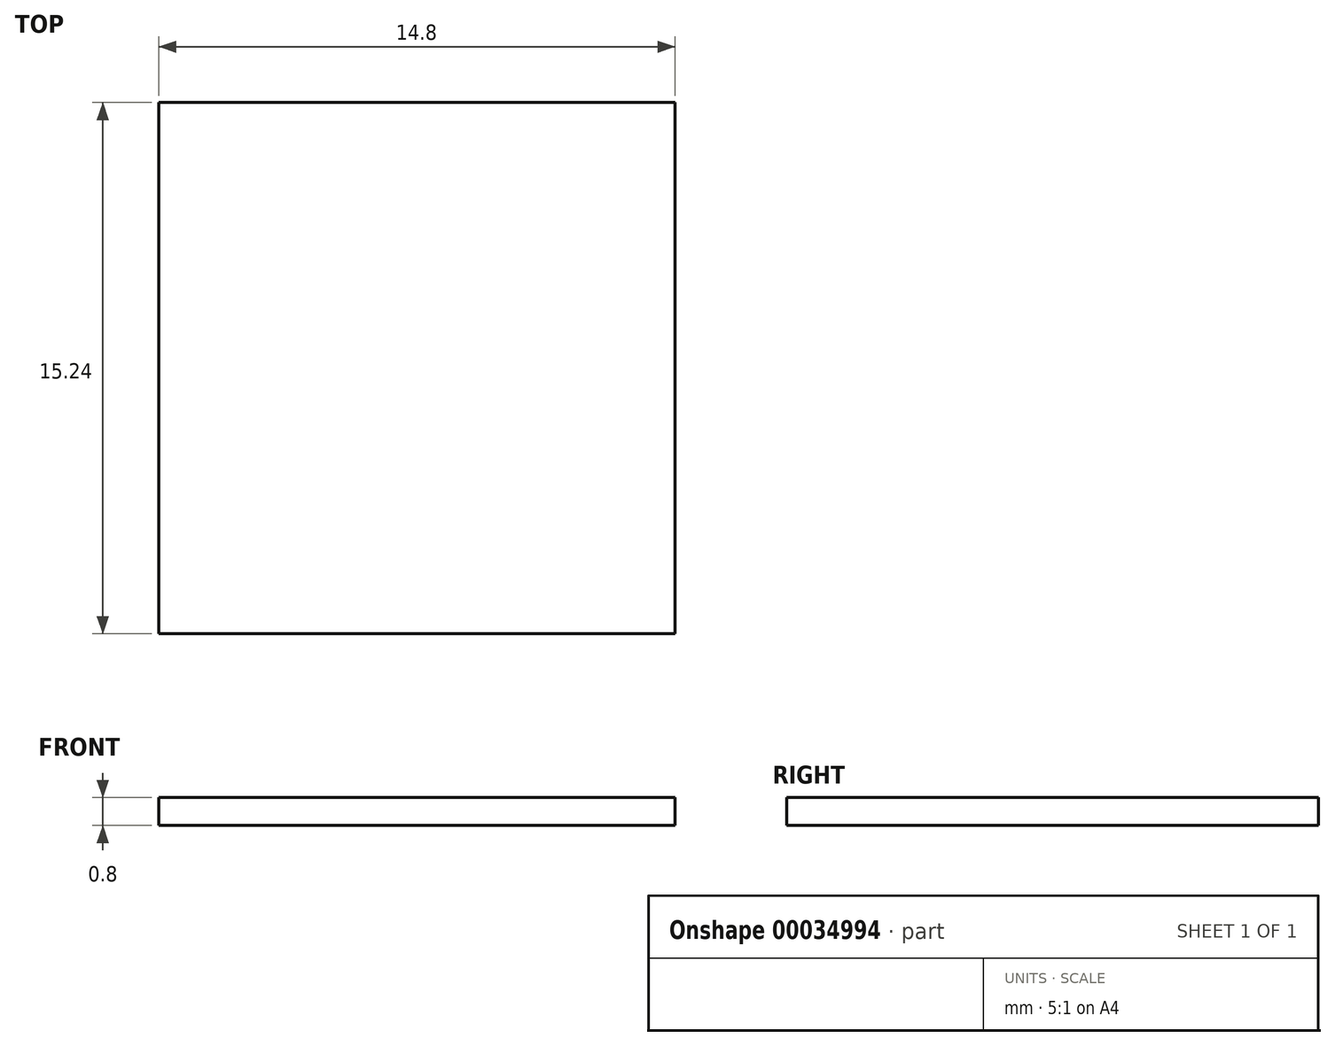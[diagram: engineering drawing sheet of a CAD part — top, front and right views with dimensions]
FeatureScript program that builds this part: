
annotation { "Feature Type Name" : "Feature", "Feature Type Description" : "" }
export const myFeature = defineFeature(function(context is Context, id is Id, definition is map)
    precondition{}
    {
        {
            var Q0;
            Q0=qCreatedBy(makeId("Top.planeOp"),FACE);
            var sketch = newSketch(context, id + "F0", { "sketchPlane" : qUnion([Q0])});
            skLineSegment(sketch, "E0.rect.bottom", {"start": v(7.4, -7.62) * mm, "end": v(-7.4, -7.62) * mm});
            skLineSegment(sketch, "E0.rect.top", {"start": v(7.4, 7.62) * mm, "end": v(-7.4, 7.62) * mm});
            skLineSegment(sketch, "E0.rect.left", {"start": v(7.4, -7.62) * mm, "end": v(7.4, 7.62) * mm});
            skLineSegment(sketch, "E0.rect.right", {"start": v(-7.4, -7.62) * mm, "end": v(-7.4, 7.62) * mm});
            skPoint(sketch, "E0.rect.middle", {"position": v(0, 0) * mm});
            skSolve(sketch);
        }
        {
            var Q0;
            Q0=makeQuery(id+"F0.imprint","IMPRINT",FACE,{"disambiguationData":[TD([[makeQuery(id+"F0.imprint","IMPRINT",EDGE,{"derivedFrom":sQuery(id+"F0.wireOp",EDGE,"E0.rect.bottom")}),-1.0]])]});
            extrude(context, id + "F1", {"entities" : qUnion([Q0]), "depth" : 0.8 * mm});
        }
    });
